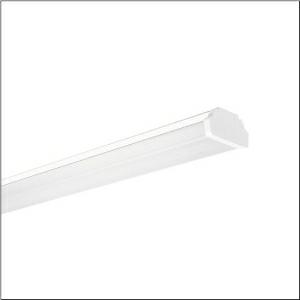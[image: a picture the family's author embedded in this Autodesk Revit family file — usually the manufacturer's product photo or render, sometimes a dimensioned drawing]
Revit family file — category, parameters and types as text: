
# Revit family: dus_r__31_gen_2_53bd812dv4d5d2_d242
name_source: partatom
category: Lighting Fixtures
units: mm (PartAtom-declared; Revit-internal decimal feet)

## family parameters
Cut with Voids When Loaded = No
Host = Face
Light Source = No
Part Type = Normal
Room Calculation Point = No
Round Connector Dimension = Use Diameter
Shared = No

## types (1)
- --- (1 x LED, 13680 lm, 74.9 W, 4000K)
    Apparent Load = 75 VA
    CIE Flux Codes = 47 80 95 93 100
    Color Rendering = 80
    Color Temperature = 4000K
    Default Elevation = 1800 mm
    Description = DUS® 31 Gen.2, luminaire insert, of sheet steel, coil coated, white, length: 1.535mm, width: 81mm, height: 90mm, 5x system unit, system units: 307mm, LED rated luminous flux: 13.680lm, light colour: 840, control gear: DALI 2, control gear: ECG DALI, with plug, 5-pole, with phase selection, mains connection: 220..240V, AC, 50/60Hz, rated input power: 75W, through-wiring accessed according to module size, primary optical cover: cover, of PMMA, light emission: direct distribution, primary light characteristic: symmetric, protection rating (complete): IP20, protection rating (LED compartment): IP50, insulation class (complete): insulation class I (protective earthing), certification: CE, ENEC, VDE, UKCA, impact resistance: IK03, permissible ambient temperature for indoor applications: -25..+35°C, corresponds to IFS (International Featured Standards) requirements for safety and quality in the food industry, reducing of maximum allowable ambient temperature of 5°C with ceiling mounting, packaging unit: 1 piece
    Height = 95 mm
    Lamp = 1 x LED
    Lamp Light Flux = 13680 lm
    Lamp Power = 74.9 W
    Lamp count = 1
    Length = 1535 mm
    Luminous efficacy = 183 lm/W
    Manufacturer = Siteco
    ModVariant = No
    Model = 53BD812DV4D5D2
    Mounting Place = Ceiling
    Mounting Type = Pendant
    Number of Poles = 1
    OnlyDefault = Yes
    Power Factor = 1
    Product Name = DUS® 31 Gen.2
    Product group = luminaire insert | ceiling pendant
    ProductGroupID = 902
    Protection Class = Protection class I
    Protection Degree = IP 20
    RLX_Detail_Level = 1
    RLX_Emergency_Light_Flux = 0 lm
    RLX_Emergency_Type = 0
    RLX_Emergency_Type_DB = No
    RlxData = <blob elided: 32145 chars, md5=935dccd8>
    Socket = socket
    Standby Power = 0 W
    System Light Flux = 13680 lm
    System Power = 75 W
    Type Comments = factory setting: luminous flux: 100 % | dim-lin: 254 | 511 mA
    Type Image = l_1319596.jpg
    URL = http://relux.com
    VarID = @adj_063183
    Voltage = 0 V
    Weight = 0.00 kg
    Width = 81 mm

## geometry (parser evidence)
native form markers: Blend x4, Sweep x13
no freeform markers — native parametric forms only
